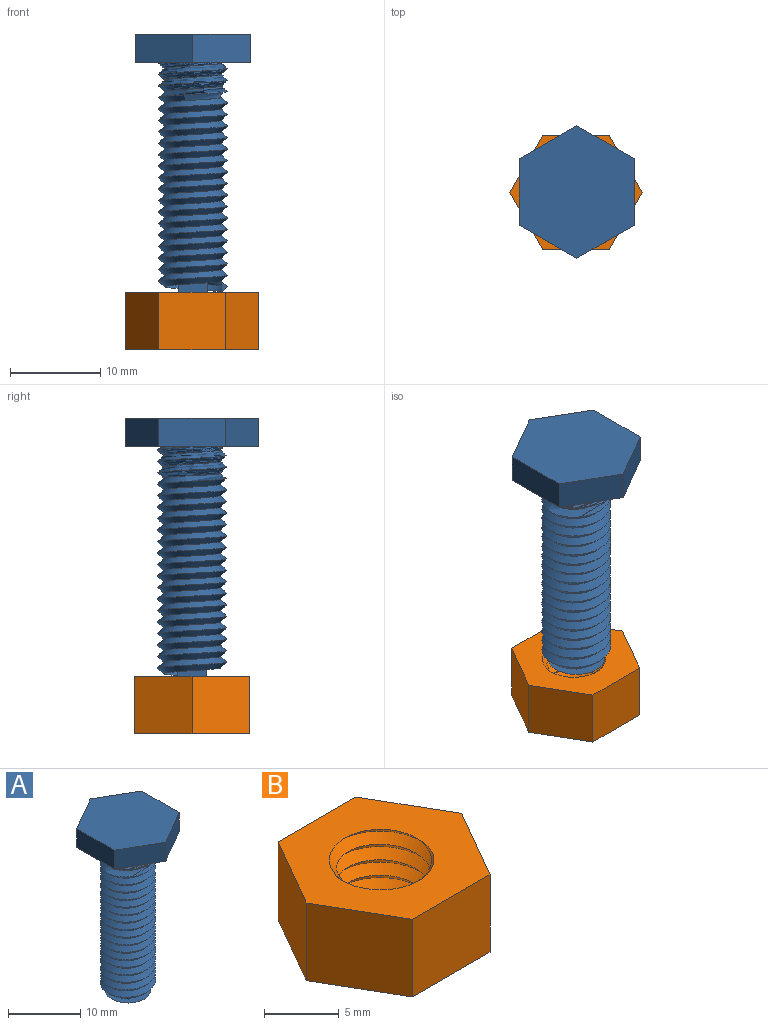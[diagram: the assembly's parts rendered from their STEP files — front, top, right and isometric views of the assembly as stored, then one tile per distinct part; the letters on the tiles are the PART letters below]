
ASSEMBLY  parts=2 mates=1
PART A: 18 faces, bbox 12.7x14.7x28.6 mm
  f0: cylinder r=3.17mm len=25.4mm, axis (0,0,1), area 13.6mm2, adj f1,f15,f16,f17
  f1: plane 6.35x6.35mm, normal (0,0,-1), area 21.6mm2, adj f0,f10,f11,f12,f13
  f2: plane 6.35x3.67mm, normal (-0.5,0.87,0), area 23.3mm2, adj f3,f7,f8,f9
  f3: plane 7.33x3.18mm, normal (-1,0,0), area 23.3mm2, adj f2,f4,f8,f9
  f4: plane 6.35x3.67mm, normal (-0.5,-0.87,0), area 23.3mm2, adj f3,f5,f8,f9
  f5: plane 6.35x3.67mm, normal (0.5,-0.87,0), area 23.3mm2, adj f4,f6,f8,f9
  f6: plane 7.33x3.18mm, normal (1,0,0), area 23.3mm2, adj f5,f7,f8,f9
  f7: plane 6.35x3.67mm, normal (0.5,0.87,0), area 23.3mm2, adj f2,f6,f8,f9
  f8: plane 14.66x12.7mm, normal (0,0,-1), area 101.3mm2, adj f2,f3,f4,f5,f6,f7,f15,f16
  f9: plane 14.66x12.7mm, normal (0,0,1), area 139.7mm2, adj f2,f3,f4,f5,f6,f7
  f10: plane 19.05x3.18mm, normal (-1,0,0), area 60.5mm2, adj f1,f11,f13,f14
  f11: plane 19.05x3.18mm, normal (0,1,0), area 60.5mm2, adj f1,f10,f12,f14
  f12: plane 19.05x3.18mm, normal (1,0,0), area 60.5mm2, adj f1,f11,f13,f14
  f13: plane 19.05x3.18mm, normal (0,-1,0), area 60.5mm2, adj f1,f10,f12,f14
  f14: plane 3.18x3.18mm, normal (0,0,-1), area 10.1mm2, adj f10,f11,f12,f13
  f15: bspline ~25.4x7.62mm, area 381mm2, adj f0,f8,f16,f17
  f16: bspline ~26.04x8.8mm, area 390.3mm2, adj f0,f8,f15,f17
  f17: plane 1.27x0.64mm, normal (0.02,-1,0), area 0.4mm2, adj f0,f15,f16
PART B: 11 faces, bbox 14.7x12.7x7.8 mm
  f0: plane 6.35x6.35mm, normal (0.87,0.5,0), area 46.6mm2, adj f1,f6,f7,f8
  f1: plane 7.33x6.35mm, normal (0,1,0), area 46.6mm2, adj f0,f2,f7,f8
  f2: plane 6.35x6.35mm, normal (-0.87,0.5,0), area 46.6mm2, adj f1,f3,f7,f8
  f3: plane 6.35x6.35mm, normal (-0.87,-0.5,0), area 46.6mm2, adj f2,f4,f7,f8
  f4: plane 7.33x6.35mm, normal (0,-1,0), area 46.6mm2, adj f3,f6,f7,f8
  f5: cylinder r=3.17mm len=0mm, axis (0,0,-1), area 0mm2, adj f7,f9
  f6: plane 6.35x6.35mm, normal (0.87,-0.5,0), area 46.6mm2, adj f0,f4,f7,f8
  f7: plane 14.66x12.7mm, normal (0,0,1), area 101.3mm2, adj f0,f1,f2,f3,f4,f5,f6,f9
  f8: plane 14.66x12.7mm, normal (0,0,-1), area 101.3mm2, adj f0,f1,f2,f3,f4,f6,f9,f10
  f9: bspline ~8.8x7.83mm, area 98.5mm2, adj f5,f7,f8,f10
  f10: bspline ~7.62x7.62mm, area 98.5mm2, adj f7,f8,f9
PLACE A at identity
PLACE B t=(-0.1,0,-34.93)mm
MATE cylindrical B.f7 <-> A.f0  axis (0,0,1) through (0,0,-28.58)mm
